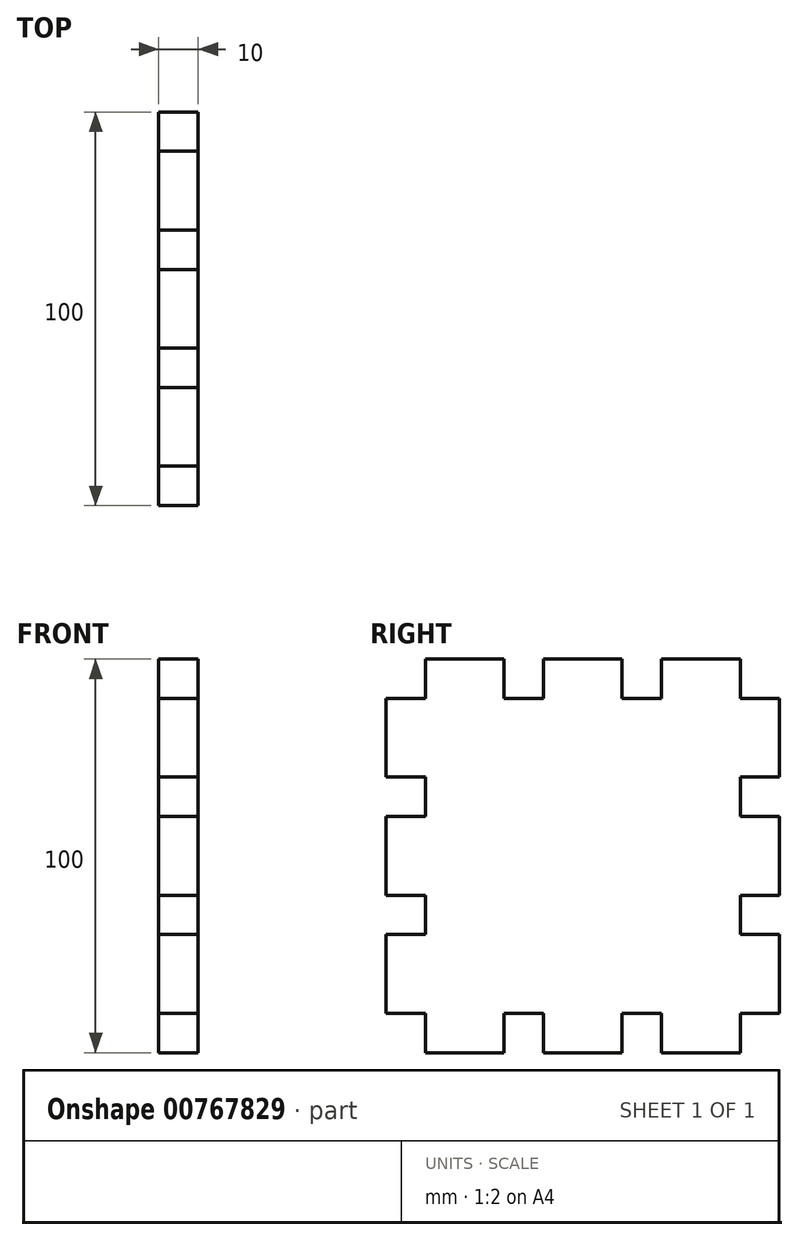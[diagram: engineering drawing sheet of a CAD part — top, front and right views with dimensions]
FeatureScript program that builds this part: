
annotation { "Feature Type Name" : "Feature", "Feature Type Description" : "" }
export const myFeature = defineFeature(function(context is Context, id is Id, definition is map)
    precondition{}
    {
        {
            var Q0;
            Q0=qCreatedBy(makeId("Right.planeOp"),FACE);
            var sketch = newSketch(context, id + "F0", { "sketchPlane" : qUnion([Q0])});
            skLineSegment(sketch, "E0.bottom", {"start": v(-26.73, 54.85) * mm, "end": v(73.27, 54.85) * mm});
            skLineSegment(sketch, "E0.top", {"start": v(-26.73, -45.15) * mm, "end": v(73.27, -45.15) * mm});
            skLineSegment(sketch, "E0.left", {"start": v(-26.73, 54.85) * mm, "end": v(-26.73, -45.15) * mm});
            skLineSegment(sketch, "E0.right", {"start": v(73.27, 54.85) * mm, "end": v(73.27, -45.15) * mm});
            skSolve(sketch);
        }
        {
            var Q0;
            Q0 = qSketchRegion(id + "F0", true);
            extrude(context, id + "F1", {"entities" : qUnion([Q0]), "depth" : 10 * mm, "offsetDistance" : 25 * mm});
        }
        {
            var Q0;
            Q0=makeQuery(id+"F1.opExtrude","CAP_FACE",FACE,{"disambiguationData":[OSD([sQuery(id+"F0.wireOp",EDGE,"E0.bottom"),sQuery(id+"F0.wireOp",EDGE,"E0.top"),sQuery(id+"F0.wireOp",EDGE,"E0.left"),sQuery(id+"F0.wireOp",EDGE,"E0.right")])],"isStart":false});
            var sketch = newSketch(context, id + "F2", { "sketchPlane" : qUnion([Q0])});
            skLineSegment(sketch, "E1.bottom", {"start": v(-26.73, 54.85) * mm, "end": v(-16.73, 54.85) * mm});
            skLineSegment(sketch, "E1.top", {"start": v(-26.73, 44.85) * mm, "end": v(-16.73, 44.85) * mm});
            skLineSegment(sketch, "E1.left", {"start": v(-26.73, 54.85) * mm, "end": v(-26.73, 44.85) * mm});
            skLineSegment(sketch, "E1.right", {"start": v(-16.73, 54.85) * mm, "end": v(-16.73, 44.85) * mm});
            skSolve(sketch);
        }
        {
            var Q0;
            Q0 = qSketchRegion(id + "F2", true);
            extrude(context, id + "F3", {"entities" : qUnion([Q0]), "operationType" : NewBodyOperationType.REMOVE, "oppositeDirection" : true, "depth" : 10 * mm, "offsetDistance" : 25 * mm});
        }
        {
            var Q0;
            Q0=makeQuery(id+"F1.opExtrude","CAP_FACE",FACE,{"disambiguationData":[OSD([sQuery(id+"F0.wireOp",EDGE,"E0.bottom"),sQuery(id+"F0.wireOp",EDGE,"E0.top"),sQuery(id+"F0.wireOp",EDGE,"E0.left"),sQuery(id+"F0.wireOp",EDGE,"E0.right")])],"isStart":false});
            var sketch = newSketch(context, id + "F4", { "sketchPlane" : qUnion([Q0])});
            skLineSegment(sketch, "E2.bottom", {"start": v(-26.73, 24.85) * mm, "end": v(-16.73, 24.85) * mm});
            skLineSegment(sketch, "E2.top", {"start": v(-26.73, 14.85) * mm, "end": v(-16.73, 14.85) * mm});
            skLineSegment(sketch, "E2.left", {"start": v(-26.73, 24.85) * mm, "end": v(-26.73, 14.85) * mm});
            skLineSegment(sketch, "E2.right", {"start": v(-16.73, 24.85) * mm, "end": v(-16.73, 14.85) * mm});
            skSolve(sketch);
        }
        {
            var Q0;
            Q0 = qSketchRegion(id + "F4", true);
            extrude(context, id + "F5", {"entities" : qUnion([Q0]), "operationType" : NewBodyOperationType.REMOVE, "oppositeDirection" : true, "depth" : 25 * mm, "offsetDistance" : 25 * mm});
        }
        {
            var Q0;
            Q0=makeQuery(id+"F1.opExtrude","CAP_FACE",FACE,{"disambiguationData":[OSD([sQuery(id+"F0.wireOp",EDGE,"E0.bottom"),sQuery(id+"F0.wireOp",EDGE,"E0.top"),sQuery(id+"F0.wireOp",EDGE,"E0.left"),sQuery(id+"F0.wireOp",EDGE,"E0.right")])],"isStart":false});
            var sketch = newSketch(context, id + "F6", { "sketchPlane" : qUnion([Q0])});
            skLineSegment(sketch, "E3.bottom", {"start": v(-26.73, -5.15) * mm, "end": v(-16.73, -5.15) * mm});
            skLineSegment(sketch, "E3.top", {"start": v(-26.73, -15.15) * mm, "end": v(-16.73, -15.15) * mm});
            skLineSegment(sketch, "E3.left", {"start": v(-26.73, -5.15) * mm, "end": v(-26.73, -15.15) * mm});
            skLineSegment(sketch, "E3.right", {"start": v(-16.73, -5.15) * mm, "end": v(-16.73, -15.15) * mm});
            skSolve(sketch);
        }
        {
            var Q0;
            Q0 = qSketchRegion(id + "F6", true);
            extrude(context, id + "F7", {"entities" : qUnion([Q0]), "operationType" : NewBodyOperationType.REMOVE, "oppositeDirection" : true, "depth" : 10 * mm, "offsetDistance" : 25 * mm});
        }
        {
            var Q0;
            Q0=makeQuery(id+"F1.opExtrude","CAP_FACE",FACE,{"disambiguationData":[OSD([sQuery(id+"F0.wireOp",EDGE,"E0.bottom"),sQuery(id+"F0.wireOp",EDGE,"E0.top"),sQuery(id+"F0.wireOp",EDGE,"E0.left"),sQuery(id+"F0.wireOp",EDGE,"E0.right")])],"isStart":false});
            var sketch = newSketch(context, id + "F8", { "sketchPlane" : qUnion([Q0])});
            skLineSegment(sketch, "E4.bottom", {"start": v(-26.73, -35.15) * mm, "end": v(-16.73, -35.15) * mm});
            skLineSegment(sketch, "E4.top", {"start": v(-26.73, -45.15) * mm, "end": v(-16.73, -45.15) * mm});
            skLineSegment(sketch, "E4.left", {"start": v(-26.73, -35.15) * mm, "end": v(-26.73, -45.15) * mm});
            skLineSegment(sketch, "E4.right", {"start": v(-16.73, -35.15) * mm, "end": v(-16.73, -45.15) * mm});
            skSolve(sketch);
        }
        {
            var Q0;
            Q0 = qSketchRegion(id + "F8", true);
            extrude(context, id + "F9", {"entities" : qUnion([Q0]), "operationType" : NewBodyOperationType.REMOVE, "oppositeDirection" : true, "depth" : 10 * mm, "offsetDistance" : 25 * mm});
        }
        {
            var Q0;
            Q0=makeQuery(id+"F1.opExtrude","CAP_FACE",FACE,{"disambiguationData":[OSD([sQuery(id+"F0.wireOp",EDGE,"E0.bottom"),sQuery(id+"F0.wireOp",EDGE,"E0.top"),sQuery(id+"F0.wireOp",EDGE,"E0.left"),sQuery(id+"F0.wireOp",EDGE,"E0.right")])],"isStart":false});
            var sketch = newSketch(context, id + "F10", { "sketchPlane" : qUnion([Q0])});
            skLineSegment(sketch, "E5.bottom", {"start": v(3.27, -45.15) * mm, "end": v(13.27, -45.15) * mm});
            skLineSegment(sketch, "E5.top", {"start": v(3.27, -35.15) * mm, "end": v(13.27, -35.15) * mm});
            skLineSegment(sketch, "E5.left", {"start": v(3.27, -45.15) * mm, "end": v(3.27, -35.15) * mm});
            skLineSegment(sketch, "E5.right", {"start": v(13.27, -45.15) * mm, "end": v(13.27, -35.15) * mm});
            skSolve(sketch);
        }
        {
            var Q0;
            Q0 = qSketchRegion(id + "F10", true);
            extrude(context, id + "F11", {"entities" : qUnion([Q0]), "operationType" : NewBodyOperationType.REMOVE, "oppositeDirection" : true, "depth" : 10 * mm, "offsetDistance" : 25 * mm});
        }
        {
            var Q0;
            Q0=makeQuery(id+"F1.opExtrude","CAP_FACE",FACE,{"disambiguationData":[OSD([sQuery(id+"F0.wireOp",EDGE,"E0.bottom"),sQuery(id+"F0.wireOp",EDGE,"E0.top"),sQuery(id+"F0.wireOp",EDGE,"E0.left"),sQuery(id+"F0.wireOp",EDGE,"E0.right")])],"isStart":false});
            var sketch = newSketch(context, id + "F12", { "sketchPlane" : qUnion([Q0])});
            skPoint(sketch, "E6.oppositeSnap0", {"position": v(8.27, -35.15) * mm});
            skLineSegment(sketch, "E6.bottom", {"start": v(33.27, -45.15) * mm, "end": v(43.27, -45.15) * mm});
            skLineSegment(sketch, "E6.top", {"start": v(33.27, -35.15) * mm, "end": v(43.27, -35.15) * mm});
            skLineSegment(sketch, "E6.left", {"start": v(33.27, -45.15) * mm, "end": v(33.27, -35.15) * mm});
            skLineSegment(sketch, "E6.right", {"start": v(43.27, -45.15) * mm, "end": v(43.27, -35.15) * mm});
            skSolve(sketch);
        }
        {
            var Q0;
            Q0 = qSketchRegion(id + "F12", true);
            extrude(context, id + "F13", {"entities" : qUnion([Q0]), "operationType" : NewBodyOperationType.REMOVE, "oppositeDirection" : true, "depth" : 10 * mm, "offsetDistance" : 25 * mm});
        }
        {
            var Q0;
            Q0=makeQuery(id+"F1.opExtrude","CAP_FACE",FACE,{"disambiguationData":[OSD([sQuery(id+"F0.wireOp",EDGE,"E0.bottom"),sQuery(id+"F0.wireOp",EDGE,"E0.top"),sQuery(id+"F0.wireOp",EDGE,"E0.left"),sQuery(id+"F0.wireOp",EDGE,"E0.right")])],"isStart":false});
            var sketch = newSketch(context, id + "F14", { "sketchPlane" : qUnion([Q0])});
            skLineSegment(sketch, "E7.bottom", {"start": v(73.27, -45.15) * mm, "end": v(63.27, -45.15) * mm});
            skLineSegment(sketch, "E7.top", {"start": v(73.27, -35.15) * mm, "end": v(63.27, -35.15) * mm});
            skLineSegment(sketch, "E7.left", {"start": v(73.27, -45.15) * mm, "end": v(73.27, -35.15) * mm});
            skLineSegment(sketch, "E7.right", {"start": v(63.27, -45.15) * mm, "end": v(63.27, -35.15) * mm});
            skSolve(sketch);
        }
        {
            var Q0;
            Q0 = qSketchRegion(id + "F14", true);
            extrude(context, id + "F15", {"entities" : qUnion([Q0]), "operationType" : NewBodyOperationType.REMOVE, "oppositeDirection" : true, "depth" : 20 * mm, "offsetDistance" : 25 * mm});
        }
        {
            var Q0;
            Q0=makeQuery(id+"F1.opExtrude","CAP_FACE",FACE,{"disambiguationData":[OSD([sQuery(id+"F0.wireOp",EDGE,"E0.bottom"),sQuery(id+"F0.wireOp",EDGE,"E0.top"),sQuery(id+"F0.wireOp",EDGE,"E0.left"),sQuery(id+"F0.wireOp",EDGE,"E0.right")])],"isStart":false});
            var sketch = newSketch(context, id + "F16", { "sketchPlane" : qUnion([Q0])});
            skLineSegment(sketch, "E8.bottom", {"start": v(73.27, -15.15) * mm, "end": v(63.27, -15.15) * mm});
            skLineSegment(sketch, "E8.top", {"start": v(73.27, -5.15) * mm, "end": v(63.27, -5.15) * mm});
            skLineSegment(sketch, "E8.left", {"start": v(73.27, -15.15) * mm, "end": v(73.27, -5.15) * mm});
            skLineSegment(sketch, "E8.right", {"start": v(63.27, -15.15) * mm, "end": v(63.27, -5.15) * mm});
            skSolve(sketch);
        }
        {
            var Q0;
            Q0 = qSketchRegion(id + "F16", true);
            extrude(context, id + "F17", {"entities" : qUnion([Q0]), "operationType" : NewBodyOperationType.REMOVE, "oppositeDirection" : true, "depth" : 10 * mm, "offsetDistance" : 25 * mm});
        }
        {
            var Q0;
            Q0=makeQuery(id+"F1.opExtrude","CAP_FACE",FACE,{"disambiguationData":[OSD([sQuery(id+"F0.wireOp",EDGE,"E0.bottom"),sQuery(id+"F0.wireOp",EDGE,"E0.top"),sQuery(id+"F0.wireOp",EDGE,"E0.left"),sQuery(id+"F0.wireOp",EDGE,"E0.right")])],"isStart":false});
            var sketch = newSketch(context, id + "F18", { "sketchPlane" : qUnion([Q0])});
            skLineSegment(sketch, "E9.bottom", {"start": v(73.27, 14.85) * mm, "end": v(63.27, 14.85) * mm});
            skLineSegment(sketch, "E9.top", {"start": v(73.27, 24.85) * mm, "end": v(63.27, 24.85) * mm});
            skLineSegment(sketch, "E9.left", {"start": v(73.27, 14.85) * mm, "end": v(73.27, 24.85) * mm});
            skLineSegment(sketch, "E9.right", {"start": v(63.27, 14.85) * mm, "end": v(63.27, 24.85) * mm});
            skSolve(sketch);
        }
        {
            var Q0;
            Q0 = qSketchRegion(id + "F18", true);
            extrude(context, id + "F19", {"entities" : qUnion([Q0]), "operationType" : NewBodyOperationType.REMOVE, "oppositeDirection" : true, "depth" : 10 * mm, "offsetDistance" : 25 * mm});
        }
        {
            var Q0;
            Q0=makeQuery(id+"F1.opExtrude","CAP_FACE",FACE,{"disambiguationData":[OSD([sQuery(id+"F0.wireOp",EDGE,"E0.bottom"),sQuery(id+"F0.wireOp",EDGE,"E0.top"),sQuery(id+"F0.wireOp",EDGE,"E0.left"),sQuery(id+"F0.wireOp",EDGE,"E0.right")])],"isStart":false});
            var sketch = newSketch(context, id + "F20", { "sketchPlane" : qUnion([Q0])});
            skLineSegment(sketch, "E10.bottom", {"start": v(73.27, 54.85) * mm, "end": v(63.27, 54.85) * mm});
            skLineSegment(sketch, "E10.top", {"start": v(73.27, 44.85) * mm, "end": v(63.27, 44.85) * mm});
            skLineSegment(sketch, "E10.left", {"start": v(73.27, 54.85) * mm, "end": v(73.27, 44.85) * mm});
            skLineSegment(sketch, "E10.right", {"start": v(63.27, 54.85) * mm, "end": v(63.27, 44.85) * mm});
            skSolve(sketch);
        }
        {
            var Q0;
            Q0 = qSketchRegion(id + "F20", true);
            extrude(context, id + "F21", {"entities" : qUnion([Q0]), "operationType" : NewBodyOperationType.REMOVE, "oppositeDirection" : true, "depth" : 10 * mm, "offsetDistance" : 25 * mm});
        }
        {
            var Q0;
            Q0=makeQuery(id+"F1.opExtrude","CAP_FACE",FACE,{"disambiguationData":[OSD([sQuery(id+"F0.wireOp",EDGE,"E0.bottom"),sQuery(id+"F0.wireOp",EDGE,"E0.top"),sQuery(id+"F0.wireOp",EDGE,"E0.left"),sQuery(id+"F0.wireOp",EDGE,"E0.right")])],"isStart":false});
            var sketch = newSketch(context, id + "F22", { "sketchPlane" : qUnion([Q0])});
            skLineSegment(sketch, "E11.bottom", {"start": v(43.27, 54.85) * mm, "end": v(33.27, 54.85) * mm});
            skLineSegment(sketch, "E11.top", {"start": v(43.27, 44.85) * mm, "end": v(33.27, 44.85) * mm});
            skLineSegment(sketch, "E11.left", {"start": v(43.27, 54.85) * mm, "end": v(43.27, 44.85) * mm});
            skLineSegment(sketch, "E11.right", {"start": v(33.27, 54.85) * mm, "end": v(33.27, 44.85) * mm});
            skSolve(sketch);
        }
        {
            var Q0;
            Q0 = qSketchRegion(id + "F22", true);
            extrude(context, id + "F23", {"entities" : qUnion([Q0]), "operationType" : NewBodyOperationType.REMOVE, "oppositeDirection" : true, "depth" : 10 * mm, "offsetDistance" : 25 * mm});
        }
        {
            var Q0;
            Q0=makeQuery(id+"F1.opExtrude","CAP_FACE",FACE,{"disambiguationData":[OSD([sQuery(id+"F0.wireOp",EDGE,"E0.bottom"),sQuery(id+"F0.wireOp",EDGE,"E0.top"),sQuery(id+"F0.wireOp",EDGE,"E0.left"),sQuery(id+"F0.wireOp",EDGE,"E0.right")])],"isStart":false});
            var sketch = newSketch(context, id + "F24", { "sketchPlane" : qUnion([Q0])});
            skLineSegment(sketch, "E12.bottom", {"start": v(13.27, 54.85) * mm, "end": v(3.27, 54.85) * mm});
            skLineSegment(sketch, "E12.top", {"start": v(13.27, 44.85) * mm, "end": v(3.27, 44.85) * mm});
            skLineSegment(sketch, "E12.left", {"start": v(13.27, 54.85) * mm, "end": v(13.27, 44.85) * mm});
            skLineSegment(sketch, "E12.right", {"start": v(3.27, 54.85) * mm, "end": v(3.27, 44.85) * mm});
            skSolve(sketch);
        }
        {
            var Q0;
            Q0 = qSketchRegion(id + "F24", true);
            extrude(context, id + "F25", {"entities" : qUnion([Q0]), "operationType" : NewBodyOperationType.REMOVE, "oppositeDirection" : true, "depth" : 10 * mm, "offsetDistance" : 25 * mm});
        }
    });
